# Revit family: Bidet-Elongated-American_Standard-Cadet-5023_Series
name_source: partatom
category: Plumbing Fixtures
revit_build: Autodesk Revit 2014 (Build: 20130308_1515(x64)
units: mm (PartAtom-declared; Revit-internal decimal feet)

## types (2) — shared parameters
ADA Compliant = Yes
Assembly Code = D2010110
Bowl Shape = Elongated
CW Connection = Yes
CWFU = 5
Cold Water Connection Diameter = 1/4"
Cold Water Connection Height = 5"
Cold Water Connection Radius = 1/8"
Cold Water Connection Width = 6"
Default Elevation = 0"
Description = Cadet Bidet
HW Connection = No
Height = 14 7/8"
Hot Water Connection Diameter = 0"
Installation Type = Floor Mounted
Left Trip Lever = Yes
Length = 25 3/4"
Manufacturer = American Standard
Price = Prices may vary. Please consult Manufacturer Representative for most up-to-date price list.
Product Documentation Link = https://www.americanstandard-us.com
Product Page URL = https://www.americanstandard-us.com
URL = https://www.americanstandard-us.com
Vent Connection = No
WFU = 5
Warranty Information = 2 Years
Waste Connection = Yes
Width = 15 3/8"
zero-valued in all types: HWFU

## per-type parameters (varying)
| type | Finish | Flush Rate | Hot Water Connection Radius | Material | Type Comments | Waste Connection Diameter | Waste Connection Radius |
| 5023.111.020 | Vitreous China-American Standard-020-White | 1.28 gpf (4.8 Lpf) | 1/8" | Vitreous China-American Standard-020-White | Available Colors: White, Bone, Linen | 1 1/4" | 5/8" |
| 5023.111.021 | Vitreous China-American Standard-021-Bone | 1.6 gpf (6.0 Lpf) | 0" | Vitreous China-American Standard-021-Bone |  | 2" | 1" |

note: column(s) folded — value = type name in every type: Model

## geometry (parser evidence)
native form markers: Sweep x2
no freeform markers — native parametric forms only
